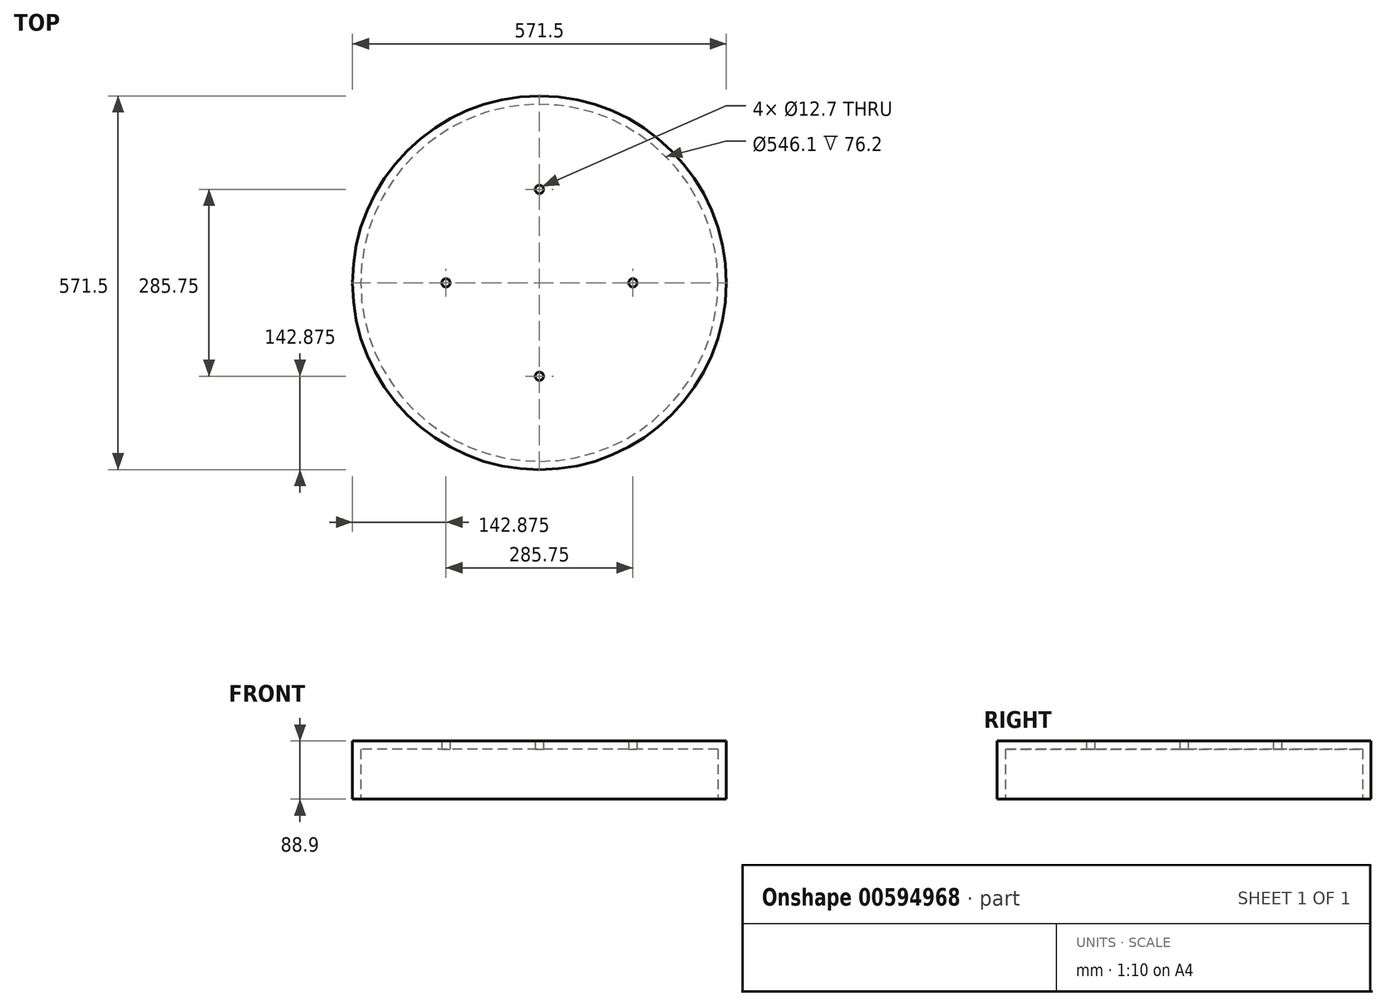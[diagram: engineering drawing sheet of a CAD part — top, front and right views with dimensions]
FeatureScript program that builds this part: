
annotation { "Feature Type Name" : "Feature", "Feature Type Description" : "" }
export const myFeature = defineFeature(function(context is Context, id is Id, definition is map)
    precondition{}
    {
        {
            var Q0;
            Q0=qCreatedBy(makeId("Top.planeOp"),FACE);
            var sketch = newSketch(context, id + "F0", { "sketchPlane" : qUnion([Q0])});
            skCircle(sketch, "E0", {"center": v(0, 0) * mm, "radius": 285.75 * mm});
            skLineSegment(sketch, "E1", {"start": v(-285.75, 0) * mm, "end": v(285.75, 0) * mm, "construction": true});
            skLineSegment(sketch, "E2", {"start": v(285.75, 0) * mm, "end": v(0, 0) * mm, "construction": true});
            skLineSegment(sketch, "E3", {"start": v(-285.75, 0) * mm, "end": v(0, 0) * mm, "construction": true});
            skLineSegment(sketch, "E4", {"start": v(0, 0) * mm, "end": v(0, 285.75) * mm, "construction": true});
            skLineSegment(sketch, "E5", {"start": v(0, 285.75) * mm, "end": v(0, 0) * mm, "construction": true});
            skLineSegment(sketch, "E6", {"start": v(0, 0) * mm, "end": v(0, -285.75) * mm, "construction": true});
            skLineSegment(sketch, "E7", {"start": v(0, -285.75) * mm, "end": v(0, 0) * mm, "construction": true});
            skLineSegment(sketch, "E8.anchor1", {"start": v(0, 0) * mm, "end": v(0, 142.87) * mm, "construction": true});
            skLineSegment(sketch, "E8.anchor2", {"start": v(0, 0) * mm, "end": v(-142.87, 0) * mm, "construction": true});
            skCircle(sketch, "E9", {"center": v(0, 142.87) * mm, "radius": 6.35 * mm});
            skCircle(sketch, "E10.1.0", {"center": v(-142.87, 0) * mm, "radius": 6.35 * mm});
            skCircle(sketch, "E10.2.0", {"center": v(0, -142.87) * mm, "radius": 6.35 * mm});
            skCircle(sketch, "E10.3.0", {"center": v(142.87, 0) * mm, "radius": 6.35 * mm});
            skSolve(sketch);
        }
        {
            var Q0;
            Q0=qSketchRegion(id+"F0",true);
            extrude(context, id + "F1", {"entities" : qUnion([Q0]), "depth" : 88.9 * mm, "offsetDistance" : 25.4 * mm});
        }
        {
            var Q0;
            Q0=makeQuery(id+"F1.opExtrude","CAP_FACE",FACE,{"disambiguationData":[OSD([sQuery(id+"F0.wireOp",EDGE,"E0")])],"isStart":true});
            shell(context, id + "F2", {"entities" : qUnion([Q0]), "thickness" : 12.7 * mm});
        }
        {
            var Q0;
            {var subQ0=sQuery(id+"F0.wireOp",EDGE,"E10.3.0");var subQ1=sQuery(id+"F0.wireOp",EDGE,"E10.2.0");var subQ2=sQuery(id+"F0.wireOp",EDGE,"E10.1.0");var subQ3=sQuery(id+"F0.wireOp",EDGE,"E9");var subQ4=sQuery(id+"F0.wireOp",EDGE,"E0");Q0=makeQuery(id+"F2.opShell","OFFSET_FACE",FACE,{"disambiguationData":[OSD([subQ4,subQ3,subQ2,subQ1,subQ0]),TDD([makeQuery(id+"F1.opExtrude","CAP_FACE",FACE,{"disambiguationData":[OSD([subQ4,subQ3,subQ2,subQ1,subQ0])],"isStart":false})])]});}
            var sketch = newSketch(context, id + "F3", { "sketchPlane" : qUnion([Q0])});
            skCircle(sketch, "E11", {"center": v(25.25, -5.05) * mm, "radius": 210.5 * mm});
            skSolve(sketch);
        }
        {
            var Q0;
            Q0=qSketchRegion(id+"F3",true);
            extrude(context, id + "F4", {"entities" : qUnion([Q0]), "operationType" : NewBodyOperationType.REMOVE, "depth" : 161.54 * mm, "offsetDistance" : 25.4 * mm});
        }
    });
